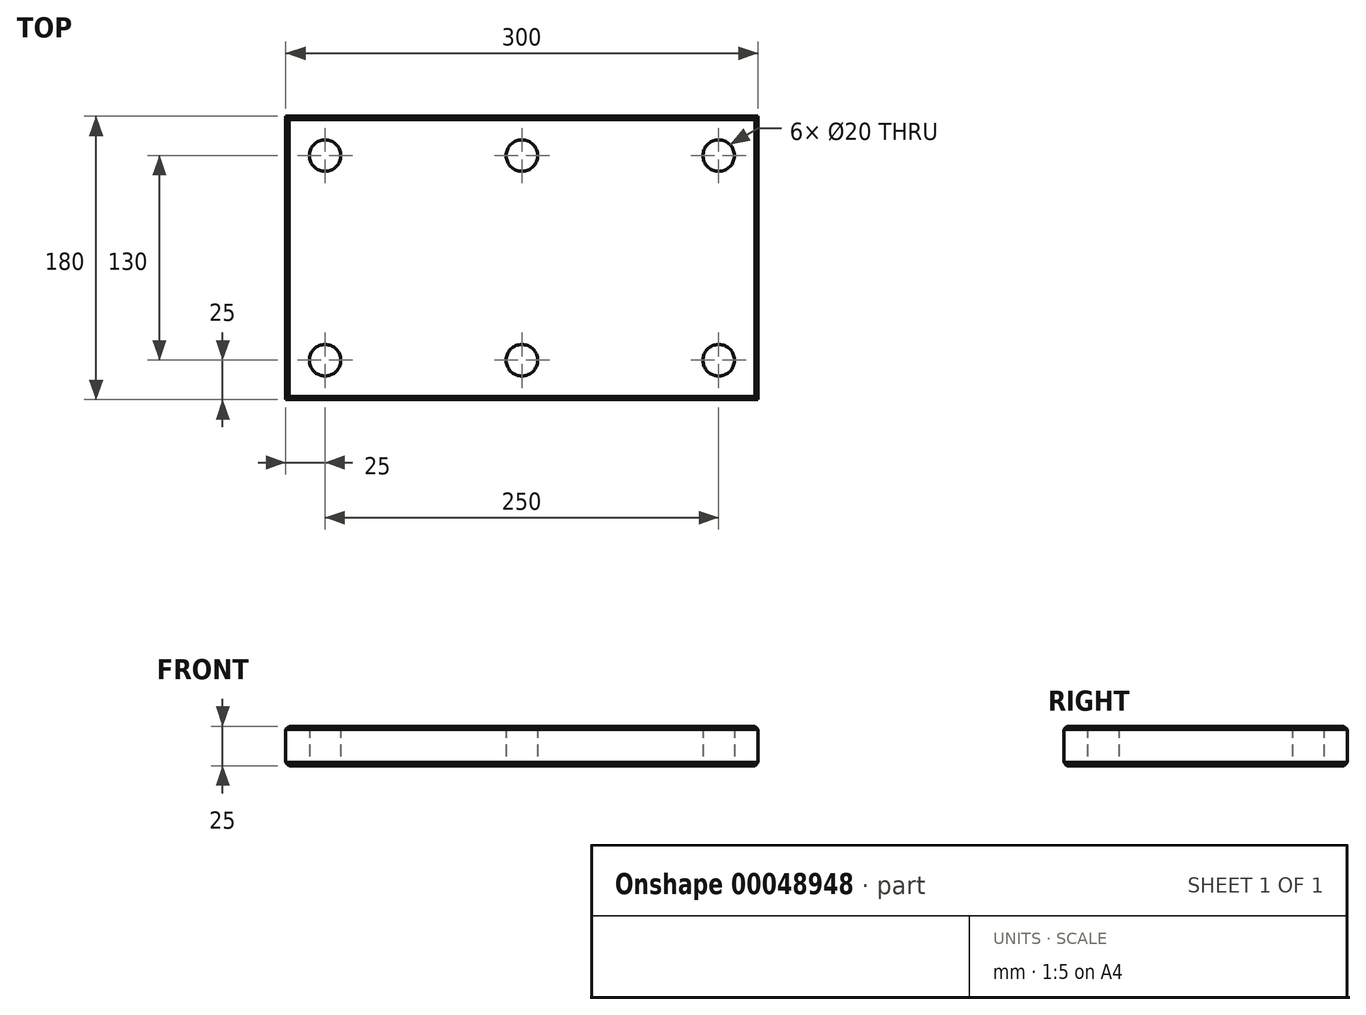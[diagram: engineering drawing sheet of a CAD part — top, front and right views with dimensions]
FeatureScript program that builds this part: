
annotation { "Feature Type Name" : "Feature", "Feature Type Description" : "" }
export const myFeature = defineFeature(function(context is Context, id is Id, definition is map)
    precondition{}
    {
        {
            var Q0;
            Q0=qCreatedBy(makeId("Top.planeOp"),FACE);
            var sketch = newSketch(context, id + "F0", { "sketchPlane" : qUnion([Q0])});
            skLineSegment(sketch, "E0.rect.bottom", {"start": v(150, 90) * mm, "end": v(-150, 90) * mm});
            skLineSegment(sketch, "E0.rect.top", {"start": v(150, -90) * mm, "end": v(-150, -90) * mm});
            skLineSegment(sketch, "E0.rect.left", {"start": v(150, 90) * mm, "end": v(150, -90) * mm});
            skLineSegment(sketch, "E0.rect.right", {"start": v(-150, 90) * mm, "end": v(-150, -90) * mm});
            skPoint(sketch, "E0.rect.middle", {"position": v(0, 0) * mm});
            skSolve(sketch);
        }
        {
            var Q0;
            Q0=makeQuery(id+"F0.imprint","IMPRINT",FACE,{"disambiguationData":[TD([[makeQuery(id+"F0.imprint","IMPRINT",EDGE,{"derivedFrom":sQuery(id+"F0.wireOp",EDGE,"E0.rect.bottom")}),1.0]])]});
            extrude(context, id + "F1", {"entities" : qUnion([Q0]), "depth" : 25 * mm});
        }
        {
            var Q0;
            Q0=makeQuery(id+"F1.opExtrude","CAP_FACE",FACE,{"disambiguationData":[OSD([sQuery(id+"F0.wireOp",EDGE,"E0.rect.bottom"),sQuery(id+"F0.wireOp",EDGE,"E0.rect.top"),sQuery(id+"F0.wireOp",EDGE,"E0.rect.left"),sQuery(id+"F0.wireOp",EDGE,"E0.rect.right")])],"isStart":true});
            var sketch = newSketch(context, id + "F2", { "sketchPlane" : qUnion([Q0])});
            skLineSegment(sketch, "E1", {"start": v(0, 90) * mm, "end": v(0, 65) * mm, "construction": true});
            skPoint(sketch, "E1.endSnap0", {"position": v(0, 90) * mm});
            skLineSegment(sketch, "E2", {"start": v(0, 65) * mm, "end": v(-125, 65) * mm, "construction": true});
            skLineSegment(sketch, "E3", {"start": v(-125, 65) * mm, "end": v(-150, 65) * mm, "construction": true});
            skLineSegment(sketch, "E4", {"start": v(0, 65) * mm, "end": v(125, 65) * mm, "construction": true});
            skCircle(sketch, "E5", {"center": v(-125, 65) * mm, "radius": 10 * mm});
            skCircle(sketch, "E6", {"center": v(0, 65) * mm, "radius": 10 * mm});
            skCircle(sketch, "E7", {"center": v(125, 65) * mm, "radius": 10 * mm});
            skLineSegment(sketch, "E8", {"start": v(-125, 65) * mm, "end": v(-125, -65) * mm, "construction": true});
            skCircle(sketch, "E9", {"center": v(-125, -65) * mm, "radius": 10 * mm});
            skCircle(sketch, "E10", {"center": v(0, -65) * mm, "radius": 10 * mm});
            skCircle(sketch, "E11", {"center": v(125, -65) * mm, "radius": 10 * mm});
            skLineSegment(sketch, "E12", {"start": v(0, 65) * mm, "end": v(0, -65) * mm, "construction": true});
            skLineSegment(sketch, "E13", {"start": v(0, -65) * mm, "end": v(125, -65) * mm, "construction": true});
            skSolve(sketch);
        }
        {
            var Q0;
            Q0=makeQuery(id+"F2.imprint","IMPRINT",FACE,{"disambiguationData":[TD([[makeQuery(id+"F2.imprint","IMPRINT",EDGE,{"derivedFrom":sQuery(id+"F2.wireOp",EDGE,"E5")}),1.0]])]});
            var Q1;
            Q1=makeQuery(id+"F2.imprint","IMPRINT",FACE,{"disambiguationData":[TD([[makeQuery(id+"F2.imprint","IMPRINT",EDGE,{"derivedFrom":sQuery(id+"F2.wireOp",EDGE,"E6")}),1.0]])]});
            var Q2;
            Q2=makeQuery(id+"F2.imprint","IMPRINT",FACE,{"disambiguationData":[TD([[makeQuery(id+"F2.imprint","IMPRINT",EDGE,{"derivedFrom":sQuery(id+"F2.wireOp",EDGE,"E7")}),1.0]])]});
            var Q3;
            Q3=makeQuery(id+"F2.imprint","IMPRINT",FACE,{"disambiguationData":[TD([[makeQuery(id+"F2.imprint","IMPRINT",EDGE,{"derivedFrom":sQuery(id+"F2.wireOp",EDGE,"E11")}),1.0]])]});
            var Q4;
            Q4=makeQuery(id+"F2.imprint","IMPRINT",FACE,{"disambiguationData":[TD([[makeQuery(id+"F2.imprint","IMPRINT",EDGE,{"derivedFrom":sQuery(id+"F2.wireOp",EDGE,"E10")}),1.0]])]});
            var Q5;
            Q5=makeQuery(id+"F2.imprint","IMPRINT",FACE,{"disambiguationData":[TD([[makeQuery(id+"F2.imprint","IMPRINT",EDGE,{"derivedFrom":sQuery(id+"F2.wireOp",EDGE,"E9")}),1.0]])]});
            extrude(context, id + "F3", {"entities" : qUnion([Q0, Q1, Q2, Q3, Q4, Q5]), "operationType" : NewBodyOperationType.REMOVE, "endBound" : BoundingType.UP_TO_NEXT, "oppositeDirection" : true, "depth" : 25 * mm});
        }
        {
            var Q0;
            Q0=makeQuery(id+"F3.boolean.opBoolean","COPY",EDGE,{"derivedFrom":makeQuery(id+"F3.opExtrude","CAP_EDGE",EDGE,{"disambiguationData":[OSD([sQuery(id+"F2.wireOp",EDGE,"E5")])],"isStart":true})});
            var Q1;
            Q1=makeQuery(id+"F3.boolean.opBoolean","COPY",EDGE,{"derivedFrom":makeQuery(id+"F3.opExtrude","CAP_EDGE",EDGE,{"disambiguationData":[OSD([sQuery(id+"F2.wireOp",EDGE,"E6")])],"isStart":true})});
            var Q2;
            Q2=makeQuery(id+"F3.boolean.opBoolean","COPY",EDGE,{"derivedFrom":makeQuery(id+"F3.opExtrude","CAP_EDGE",EDGE,{"disambiguationData":[OSD([sQuery(id+"F2.wireOp",EDGE,"E7")])],"isStart":true})});
            var Q3;
            Q3=makeQuery(id+"F3.boolean.opBoolean","COPY",EDGE,{"derivedFrom":makeQuery(id+"F3.opExtrude","CAP_EDGE",EDGE,{"disambiguationData":[OSD([sQuery(id+"F2.wireOp",EDGE,"E11")])],"isStart":true})});
            var Q4;
            Q4=makeQuery(id+"F3.boolean.opBoolean","COPY",EDGE,{"derivedFrom":makeQuery(id+"F3.opExtrude","CAP_EDGE",EDGE,{"disambiguationData":[OSD([sQuery(id+"F2.wireOp",EDGE,"E10")])],"isStart":true})});
            var Q5;
            Q5=makeQuery(id+"F3.boolean.opBoolean","COPY",EDGE,{"derivedFrom":makeQuery(id+"F3.opExtrude","CAP_EDGE",EDGE,{"disambiguationData":[OSD([sQuery(id+"F2.wireOp",EDGE,"E9")])],"isStart":true})});
            var Q6;
            Q6=makeQuery(id+"F1.opExtrude","CAP_EDGE",EDGE,{"disambiguationData":[OSD([sQuery(id+"F0.wireOp",EDGE,"E0.rect.right")])],"isStart":true});
            var Q7;
            Q7=makeQuery(id+"F1.opExtrude","CAP_EDGE",EDGE,{"disambiguationData":[OSD([sQuery(id+"F0.wireOp",EDGE,"E0.rect.bottom")])],"isStart":true});
            var Q8;
            Q8=makeQuery(id+"F1.opExtrude","CAP_EDGE",EDGE,{"disambiguationData":[OSD([sQuery(id+"F0.wireOp",EDGE,"E0.rect.right")])],"isStart":false});
            var Q9;
            Q9=makeQuery(id+"F1.opExtrude","CAP_EDGE",EDGE,{"disambiguationData":[OSD([sQuery(id+"F0.wireOp",EDGE,"E0.rect.bottom")])],"isStart":false});
            var Q10;
            Q10=makeQuery(id+"F1.opExtrude","CAP_EDGE",EDGE,{"disambiguationData":[OSD([sQuery(id+"F0.wireOp",EDGE,"E0.rect.top")])],"isStart":true});
            var Q11;
            Q11=makeQuery(id+"F1.opExtrude","CAP_EDGE",EDGE,{"disambiguationData":[OSD([sQuery(id+"F0.wireOp",EDGE,"E0.rect.left")])],"isStart":true});
            var Q12;
            Q12=makeQuery(id+"F1.opExtrude","CAP_EDGE",EDGE,{"disambiguationData":[OSD([sQuery(id+"F0.wireOp",EDGE,"E0.rect.left")])],"isStart":false});
            var Q13;
            Q13=makeQuery(id+"F1.opExtrude","CAP_EDGE",EDGE,{"disambiguationData":[OSD([sQuery(id+"F0.wireOp",EDGE,"E0.rect.top")])],"isStart":false});
            var Q14;
            Q14=makeQuery(id+"F3.boolean.opBoolean","COPY",EDGE,{"derivedFrom":makeQuery(id+"F3.opExtrude","CAP_EDGE",EDGE,{"disambiguationData":[OSD([sQuery(id+"F2.wireOp",EDGE,"E10")])],"isStart":false})});
            var Q15;
            Q15=makeQuery(id+"F3.boolean.opBoolean","COPY",EDGE,{"derivedFrom":makeQuery(id+"F3.opExtrude","CAP_EDGE",EDGE,{"disambiguationData":[OSD([sQuery(id+"F2.wireOp",EDGE,"E9")])],"isStart":false})});
            var Q16;
            Q16=makeQuery(id+"F3.boolean.opBoolean","COPY",EDGE,{"derivedFrom":makeQuery(id+"F3.opExtrude","CAP_EDGE",EDGE,{"disambiguationData":[OSD([sQuery(id+"F2.wireOp",EDGE,"E5")])],"isStart":false})});
            var Q17;
            Q17=makeQuery(id+"F3.boolean.opBoolean","COPY",EDGE,{"derivedFrom":makeQuery(id+"F3.opExtrude","CAP_EDGE",EDGE,{"disambiguationData":[OSD([sQuery(id+"F2.wireOp",EDGE,"E6")])],"isStart":false})});
            var Q18;
            Q18=makeQuery(id+"F3.boolean.opBoolean","COPY",EDGE,{"derivedFrom":makeQuery(id+"F3.opExtrude","CAP_EDGE",EDGE,{"disambiguationData":[OSD([sQuery(id+"F2.wireOp",EDGE,"E11")])],"isStart":false})});
            var Q19;
            Q19=makeQuery(id+"F3.boolean.opBoolean","COPY",EDGE,{"derivedFrom":makeQuery(id+"F3.opExtrude","CAP_EDGE",EDGE,{"disambiguationData":[OSD([sQuery(id+"F2.wireOp",EDGE,"E7")])],"isStart":false})});
            chamfer(context, id + "F4", {"entities" : qUnion([Q0, Q1, Q2, Q3, Q4, Q5, Q6, Q7, Q8, Q9, Q10, Q11, Q12, Q13, Q14, Q15, Q16, Q17, Q18, Q19]), "chamferType" : ChamferType.OFFSET_ANGLE, "width" : 2 * mm, "oppositeDirection" : false, "angle" : 45 * degree, "tangentPropagation" : true});
        }
    });
